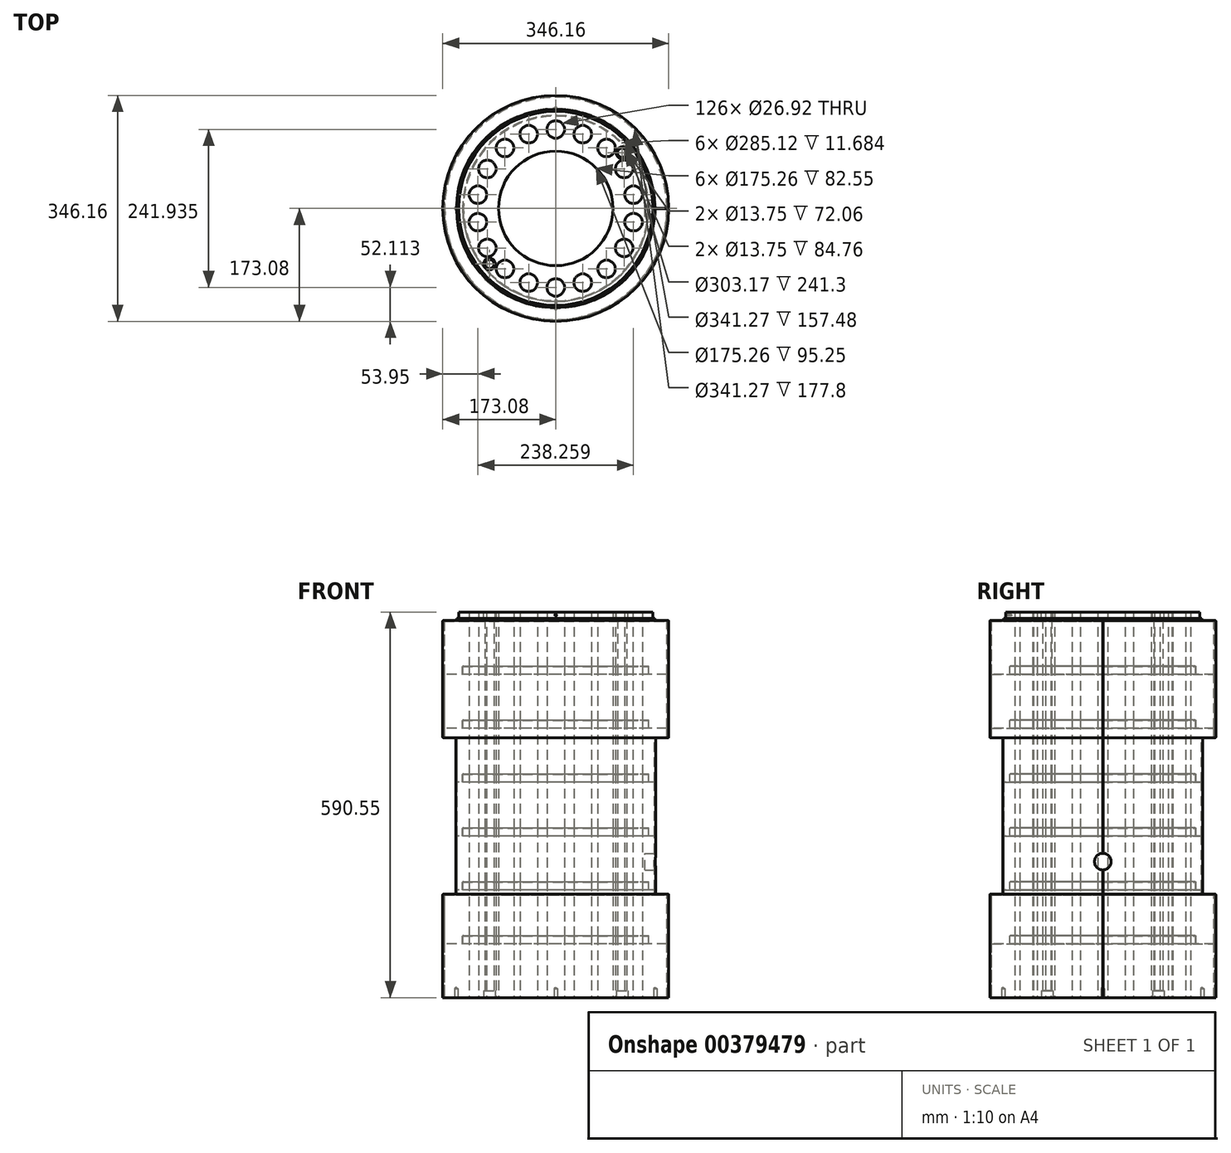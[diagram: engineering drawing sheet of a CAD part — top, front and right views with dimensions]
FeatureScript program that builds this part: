
annotation { "Feature Type Name" : "Feature", "Feature Type Description" : "" }
export const myFeature = defineFeature(function(context is Context, id is Id, definition is map)
    precondition{}
    {
        {
            var Q0;
            Q0=qCreatedBy(makeId("Right.planeOp"),FACE);
            var sketch = newSketch(context, id + "F0", { "sketchPlane" : qUnion([Q0])});
            skLineSegment(sketch, "E0", {"start": v(0, 0) * mm, "end": v(170.18, 0) * mm});
            skLineSegment(sketch, "E1", {"start": v(170.18, 157.48) * mm, "end": v(151.13, 157.48) * mm});
            skLineSegment(sketch, "E2", {"start": v(151.13, 157.48) * mm, "end": v(151.13, 398.78) * mm});
            skLineSegment(sketch, "E3", {"start": v(151.13, 398.78) * mm, "end": v(170.18, 398.78) * mm});
            skLineSegment(sketch, "E4", {"start": v(170.18, 398.78) * mm, "end": v(170.18, 576.58) * mm});
            skLineSegment(sketch, "E5", {"start": v(170.18, 576.58) * mm, "end": v(151.13, 576.58) * mm});
            skLineSegment(sketch, "E6", {"start": v(151.13, 576.58) * mm, "end": v(151.13, 581.03) * mm});
            skLineSegment(sketch, "E7", {"start": v(151.13, 581.03) * mm, "end": v(148.59, 581.03) * mm});
            skLineSegment(sketch, "E8", {"start": v(148.59, 581.03) * mm, "end": v(148.59, 590.55) * mm});
            skLineSegment(sketch, "E9", {"start": v(148.59, 590.55) * mm, "end": v(0, 590.55) * mm});
            skLineSegment(sketch, "E10", {"start": v(0, 590.55) * mm, "end": v(0, 0) * mm});
            skLineSegment(sketch, "E11", {"start": v(170.18, 82.55) * mm, "end": v(142.43, 82.55) * mm});
            skLineSegment(sketch, "E12", {"start": v(142.43, 82.55) * mm, "end": v(142.43, 95.25) * mm});
            skLineSegment(sketch, "E13", {"start": v(142.43, 95.25) * mm, "end": v(0, 95.25) * mm});
            skLineSegment(sketch, "E14", {"start": v(151.13, 165.1) * mm, "end": v(142.43, 165.1) * mm});
            skLineSegment(sketch, "E15", {"start": v(142.43, 165.1) * mm, "end": v(142.43, 177.8) * mm});
            skLineSegment(sketch, "E16", {"start": v(142.43, 177.8) * mm, "end": v(0, 177.8) * mm});
            skLineSegment(sketch, "E17", {"start": v(142.56, 82.55) * mm, "end": v(142.43, 82.55) * mm});
            skLineSegment(sketch, "E18", {"start": v(142.56, 82.55) * mm, "end": v(142.56, 95.25) * mm});
            skLineSegment(sketch, "E19", {"start": v(142.43, 165.1) * mm, "end": v(142.43, 165.1) * mm});
            skLineSegment(sketch, "E20", {"start": v(142.56, 95.25) * mm, "end": v(142.43, 95.25) * mm});
            skLineSegment(sketch, "E21", {"start": v(142.43, 177.8) * mm, "end": v(142.56, 177.8) * mm});
            skLineSegment(sketch, "E22", {"start": v(142.56, 177.8) * mm, "end": v(142.56, 165.1) * mm});
            skLineSegment(sketch, "E23", {"start": v(170.18, 412.75) * mm, "end": v(142.56, 412.75) * mm});
            skLineSegment(sketch, "E24", {"start": v(142.56, 412.75) * mm, "end": v(142.56, 425.45) * mm});
            skLineSegment(sketch, "E25", {"start": v(142.56, 425.45) * mm, "end": v(0, 425.45) * mm});
            skLineSegment(sketch, "E26", {"start": v(142.56, 412.75) * mm, "end": v(142.43, 412.75) * mm});
            skLineSegment(sketch, "E27", {"start": v(142.43, 412.75) * mm, "end": v(142.43, 425.45) * mm});
            skLineSegment(sketch, "E28", {"start": v(170.18, 495.3) * mm, "end": v(142.56, 495.3) * mm});
            skLineSegment(sketch, "E29", {"start": v(142.56, 495.3) * mm, "end": v(142.56, 508) * mm});
            skLineSegment(sketch, "E30", {"start": v(142.56, 508) * mm, "end": v(0, 508) * mm});
            skLineSegment(sketch, "E31", {"start": v(142.56, 495.3) * mm, "end": v(142.43, 495.3) * mm});
            skLineSegment(sketch, "E32", {"start": v(142.43, 495.3) * mm, "end": v(142.43, 508) * mm});
            skLineSegment(sketch, "E33", {"start": v(170.18, 0) * mm, "end": v(170.18, 82.55) * mm});
            skLineSegment(sketch, "E34", {"start": v(170.18, 82.55) * mm, "end": v(170.18, 157.48) * mm});
            skPoint(sketch, "E35.end.orphan", {"position": v(0, 177.8) * mm});
            skPoint(sketch, "E36.orphan", {"position": v(151.13, 165.1) * mm});
            skLineSegment(sketch, "E37", {"start": v(151.13, 247.65) * mm, "end": v(142.43, 247.65) * mm});
            skLineSegment(sketch, "E38", {"start": v(142.43, 247.65) * mm, "end": v(142.43, 260.35) * mm});
            skLineSegment(sketch, "E39", {"start": v(142.43, 260.35) * mm, "end": v(0, 260.35) * mm});
            skLineSegment(sketch, "E40", {"start": v(142.43, 260.35) * mm, "end": v(142.56, 260.35) * mm});
            skLineSegment(sketch, "E41", {"start": v(142.56, 260.35) * mm, "end": v(142.56, 247.65) * mm});
            skLineSegment(sketch, "E42", {"start": v(151.13, 330.2) * mm, "end": v(142.43, 330.2) * mm});
            skLineSegment(sketch, "E43", {"start": v(142.43, 330.2) * mm, "end": v(142.43, 342.9) * mm});
            skLineSegment(sketch, "E44", {"start": v(142.43, 342.9) * mm, "end": v(0, 342.9) * mm});
            skLineSegment(sketch, "E45", {"start": v(142.43, 342.9) * mm, "end": v(142.56, 342.9) * mm});
            skLineSegment(sketch, "E46", {"start": v(142.56, 342.9) * mm, "end": v(142.56, 330.2) * mm});
            skSolve(sketch);
        }
        {
            var Q0;
            {var subQ0=sQuery(id+"F0.wireOp",EDGE,"E0");Q0=makeQuery(id+"F0.imprint","IMPRINT",FACE,{"disambiguationData":[TD([[makeQuery(id+"F0.imprint","IMPRINT",EDGE,{"derivedFrom":subQ0}),1.0]])]});}
            var Q1;
            Q1=sQuery(id+"F0.wireOp",EDGE,"E10");
            revolve(context, id + "F1", {"entities" : qUnion([Q0]), "axis" : qUnion([Q1]), "revolveType" : RevolveType.FULL});
        }
        {
            var Q0;
            {var subQ6=sQuery(id+"F0.wireOp",EDGE,"E1");Q0=makeQuery(id+"F0.imprint","IMPRINT",FACE,{"disambiguationData":[TD([[makeQuery(id+"F0.imprint","IMPRINT",EDGE,{"derivedFrom":subQ6}),1.0]])]});}
            var Q1;
            Q1=sQuery(id+"F0.wireOp",EDGE,"E10");
            revolve(context, id + "F2", {"entities" : qUnion([Q0]), "axis" : qUnion([Q1]), "revolveType" : RevolveType.FULL});
        }
        {
            var Q0;
            {var subQ0=sQuery(id+"F0.wireOp",EDGE,"E16");Q0=makeQuery(id+"F0.imprint","IMPRINT",FACE,{"disambiguationData":[TD([[makeQuery(id+"F0.imprint","IMPRINT",EDGE,{"derivedFrom":subQ0}),-1.0]])]});}
            var Q1;
            Q1=sQuery(id+"F0.wireOp",EDGE,"E10");
            revolve(context, id + "F3", {"entities" : qUnion([Q0]), "axis" : qUnion([Q1]), "revolveType" : RevolveType.FULL});
        }
        {
            var Q0;
            {var subQ0=sQuery(id+"F0.wireOp",EDGE,"E39");Q0=makeQuery(id+"F0.imprint","IMPRINT",FACE,{"disambiguationData":[TD([[makeQuery(id+"F0.imprint","IMPRINT",EDGE,{"derivedFrom":subQ0}),-1.0]])]});}
            var Q1;
            Q1=sQuery(id+"F0.wireOp",EDGE,"E10");
            revolve(context, id + "F4", {"entities" : qUnion([Q0]), "axis" : qUnion([Q1]), "revolveType" : RevolveType.FULL});
        }
        {
            var Q0;
            {var subQ10=sQuery(id+"F0.wireOp",EDGE,"E3");Q0=makeQuery(id+"F0.imprint","IMPRINT",FACE,{"disambiguationData":[TD([[makeQuery(id+"F0.imprint","IMPRINT",EDGE,{"derivedFrom":subQ10}),1.0]])]});}
            var Q1;
            Q1=sQuery(id+"F0.wireOp",EDGE,"E10");
            revolve(context, id + "F5", {"entities" : qUnion([Q0]), "axis" : qUnion([Q1]), "revolveType" : RevolveType.FULL});
        }
        {
            var Q0;
            {var subQ1=sQuery(id+"F0.wireOp",EDGE,"E23");Q0=makeQuery(id+"F0.imprint","IMPRINT",FACE,{"disambiguationData":[TD([[makeQuery(id+"F0.imprint","IMPRINT",EDGE,{"derivedFrom":subQ1}),-1.0]])]});}
            var Q1;
            Q1=sQuery(id+"F0.wireOp",EDGE,"E10");
            revolve(context, id + "F6", {"entities" : qUnion([Q0]), "axis" : qUnion([Q1]), "revolveType" : RevolveType.FULL});
        }
        {
            var Q0;
            {var subQ7=sQuery(id+"F0.wireOp",EDGE,"E5");Q0=makeQuery(id+"F0.imprint","IMPRINT",FACE,{"disambiguationData":[TD([[makeQuery(id+"F0.imprint","IMPRINT",EDGE,{"derivedFrom":subQ7}),1.0]])]});}
            var Q1;
            Q1=sQuery(id+"F0.wireOp",EDGE,"E10");
            revolve(context, id + "F7", {"entities" : qUnion([Q0]), "axis" : qUnion([Q1]), "revolveType" : RevolveType.FULL});
        }
        {
            var Q0;
            Q0=makeQuery(id+"F1.opRevolve","SWEPT_FACE",FACE,{"disambiguationData":[OSD([sQuery(id+"F0.wireOp",EDGE,"E0")])]});
            var sketch = newSketch(context, id + "F8", { "sketchPlane" : qUnion([Q0])});
            skCircle(sketch, "E47", {"center": v(0, 0) * mm, "radius": 87.63 * mm});
            skCircle(sketch, "E48", {"center": v(0, -120.97) * mm, "radius": 13.46 * mm});
            skCircle(sketch, "E49", {"center": v(0, 0) * mm, "radius": 120.97 * mm, "construction": true});
            skCircle(sketch, "E50.1.0", {"center": v(41.37, -113.67) * mm, "radius": 13.46 * mm});
            skCircle(sketch, "E50.2.0", {"center": v(77.76, -92.67) * mm, "radius": 13.46 * mm});
            skCircle(sketch, "E50.3.0", {"center": v(104.76, -60.48) * mm, "radius": 13.46 * mm});
            skCircle(sketch, "E50.4.0", {"center": v(119.13, -21) * mm, "radius": 13.46 * mm});
            skCircle(sketch, "E50.5.0", {"center": v(119.13, 21) * mm, "radius": 13.46 * mm});
            skCircle(sketch, "E50.6.0", {"center": v(104.76, 60.48) * mm, "radius": 13.46 * mm});
            skCircle(sketch, "E50.7.0", {"center": v(77.76, 92.67) * mm, "radius": 13.46 * mm});
            skCircle(sketch, "E50.8.0", {"center": v(41.37, 113.67) * mm, "radius": 13.46 * mm});
            skCircle(sketch, "E50.9.0", {"center": v(0, 120.97) * mm, "radius": 13.46 * mm});
            skCircle(sketch, "E50.10.0", {"center": v(-41.37, 113.67) * mm, "radius": 13.46 * mm});
            skCircle(sketch, "E50.11.0", {"center": v(-77.76, 92.67) * mm, "radius": 13.46 * mm});
            skCircle(sketch, "E50.12.0", {"center": v(-104.76, 60.48) * mm, "radius": 13.46 * mm});
            skCircle(sketch, "E50.13.0", {"center": v(-119.13, 21) * mm, "radius": 13.46 * mm});
            skCircle(sketch, "E50.14.0", {"center": v(-119.13, -21) * mm, "radius": 13.46 * mm});
            skCircle(sketch, "E50.15.0", {"center": v(-104.76, -60.48) * mm, "radius": 13.46 * mm});
            skCircle(sketch, "E50.16.0", {"center": v(-77.76, -92.67) * mm, "radius": 13.46 * mm});
            skCircle(sketch, "E50.17.0", {"center": v(-41.37, -113.67) * mm, "radius": 13.46 * mm});
            skLineSegment(sketch, "E51", {"start": v(0, 0) * mm, "end": v(101.5, -85.17) * mm, "construction": true});
            skCircle(sketch, "E52", {"center": v(0, 0) * mm, "radius": 132.5 * mm, "construction": true});
            skCircle(sketch, "E53", {"center": v(101.5, -85.17) * mm, "radius": 6.87 * mm});
            skCircle(sketch, "E54.1.0", {"center": v(-101.5, 85.17) * mm, "radius": 6.87 * mm});
            skLineSegment(sketch, "E55", {"start": v(0, 0) * mm, "end": v(0, -120.97) * mm, "construction": true});
            skSolve(sketch);
        }
        {
            var Q0;
            Q0=makeQuery(id+"F8.imprint","IMPRINT",FACE,{"disambiguationData":[TD([[makeQuery(id+"F8.imprint","IMPRINT",EDGE,{"derivedFrom":sQuery(id+"F8.wireOp",EDGE,"E47")}),1.0]])]});
            var Q1;
            Q1=makeQuery(id+"F8.imprint","IMPRINT",FACE,{"disambiguationData":[TD([[makeQuery(id+"F8.imprint","IMPRINT",EDGE,{"derivedFrom":sQuery(id+"F8.wireOp",EDGE,"E48")}),1.0]])]});
            var Q2;
            Q2=makeQuery(id+"F8.imprint","IMPRINT",FACE,{"disambiguationData":[TD([[makeQuery(id+"F8.imprint","IMPRINT",EDGE,{"derivedFrom":sQuery(id+"F8.wireOp",EDGE,"E50.1.0")}),1.0]])]});
            var Q3;
            Q3=makeQuery(id+"F8.imprint","IMPRINT",FACE,{"disambiguationData":[TD([[makeQuery(id+"F8.imprint","IMPRINT",EDGE,{"derivedFrom":sQuery(id+"F8.wireOp",EDGE,"E50.17.0")}),1.0]])]});
            var Q4;
            Q4=makeQuery(id+"F8.imprint","IMPRINT",FACE,{"disambiguationData":[TD([[makeQuery(id+"F8.imprint","IMPRINT",EDGE,{"derivedFrom":sQuery(id+"F8.wireOp",EDGE,"E50.16.0")}),1.0]])]});
            var Q5;
            Q5=makeQuery(id+"F8.imprint","IMPRINT",FACE,{"disambiguationData":[TD([[makeQuery(id+"F8.imprint","IMPRINT",EDGE,{"derivedFrom":sQuery(id+"F8.wireOp",EDGE,"E53")}),1.0]])]});
            var Q6;
            Q6=makeQuery(id+"F8.imprint","IMPRINT",FACE,{"disambiguationData":[TD([[makeQuery(id+"F8.imprint","IMPRINT",EDGE,{"derivedFrom":sQuery(id+"F8.wireOp",EDGE,"E50.15.0")}),1.0]])]});
            var Q7;
            Q7=makeQuery(id+"F8.imprint","IMPRINT",FACE,{"disambiguationData":[TD([[makeQuery(id+"F8.imprint","IMPRINT",EDGE,{"derivedFrom":sQuery(id+"F8.wireOp",EDGE,"E50.14.0")}),1.0]])]});
            var Q8;
            Q8=makeQuery(id+"F8.imprint","IMPRINT",FACE,{"disambiguationData":[TD([[makeQuery(id+"F8.imprint","IMPRINT",EDGE,{"derivedFrom":sQuery(id+"F8.wireOp",EDGE,"E50.13.0")}),1.0]])]});
            var Q9;
            Q9=makeQuery(id+"F8.imprint","IMPRINT",FACE,{"disambiguationData":[TD([[makeQuery(id+"F8.imprint","IMPRINT",EDGE,{"derivedFrom":sQuery(id+"F8.wireOp",EDGE,"E50.12.0")}),1.0]])]});
            var Q10;
            Q10=makeQuery(id+"F8.imprint","IMPRINT",FACE,{"disambiguationData":[TD([[makeQuery(id+"F8.imprint","IMPRINT",EDGE,{"derivedFrom":sQuery(id+"F8.wireOp",EDGE,"E50.10.0")}),1.0]])]});
            var Q11;
            Q11=makeQuery(id+"F8.imprint","IMPRINT",FACE,{"disambiguationData":[TD([[makeQuery(id+"F8.imprint","IMPRINT",EDGE,{"derivedFrom":sQuery(id+"F8.wireOp",EDGE,"E50.9.0")}),1.0]])]});
            var Q12;
            Q12=makeQuery(id+"F8.imprint","IMPRINT",FACE,{"disambiguationData":[TD([[makeQuery(id+"F8.imprint","IMPRINT",EDGE,{"derivedFrom":sQuery(id+"F8.wireOp",EDGE,"E50.8.0")}),1.0]])]});
            var Q13;
            Q13=makeQuery(id+"F8.imprint","IMPRINT",FACE,{"disambiguationData":[TD([[makeQuery(id+"F8.imprint","IMPRINT",EDGE,{"derivedFrom":sQuery(id+"F8.wireOp",EDGE,"E50.6.0")}),1.0]])]});
            var Q14;
            Q14=makeQuery(id+"F8.imprint","IMPRINT",FACE,{"disambiguationData":[TD([[makeQuery(id+"F8.imprint","IMPRINT",EDGE,{"derivedFrom":sQuery(id+"F8.wireOp",EDGE,"E54.1.0")}),1.0]])]});
            var Q15;
            Q15=makeQuery(id+"F8.imprint","IMPRINT",FACE,{"disambiguationData":[TD([[makeQuery(id+"F8.imprint","IMPRINT",EDGE,{"derivedFrom":sQuery(id+"F8.wireOp",EDGE,"E50.5.0")}),1.0]])]});
            var Q16;
            Q16=makeQuery(id+"F8.imprint","IMPRINT",FACE,{"disambiguationData":[TD([[makeQuery(id+"F8.imprint","IMPRINT",EDGE,{"derivedFrom":sQuery(id+"F8.wireOp",EDGE,"E50.4.0")}),1.0]])]});
            var Q17;
            Q17=makeQuery(id+"F8.imprint","IMPRINT",FACE,{"disambiguationData":[TD([[makeQuery(id+"F8.imprint","IMPRINT",EDGE,{"derivedFrom":sQuery(id+"F8.wireOp",EDGE,"E50.2.0")}),1.0]])]});
            var Q18;
            Q18=makeQuery(id+"F8.imprint","IMPRINT",FACE,{"disambiguationData":[TD([[makeQuery(id+"F8.imprint","IMPRINT",EDGE,{"derivedFrom":sQuery(id+"F8.wireOp",EDGE,"E50.3.0")}),1.0]])]});
            var Q19;
            Q19=makeQuery(id+"F8.imprint","IMPRINT",FACE,{"disambiguationData":[TD([[makeQuery(id+"F8.imprint","IMPRINT",EDGE,{"derivedFrom":sQuery(id+"F8.wireOp",EDGE,"E50.11.0")}),1.0]])]});
            var Q20;
            Q20=makeQuery(id+"F8.imprint","IMPRINT",FACE,{"disambiguationData":[TD([[makeQuery(id+"F8.imprint","IMPRINT",EDGE,{"derivedFrom":sQuery(id+"F8.wireOp",EDGE,"E50.7.0")}),1.0]])]});
            var Q21;
            Q21=makeQuery(id+"F7.opRevolve","SWEPT_FACE",FACE,{"disambiguationData":[OSD([sQuery(id+"F0.wireOp",EDGE,"E9")])]});
            extrude(context, id + "F9", {"entities" : qUnion([Q0, Q1, Q2, Q3, Q4, Q5, Q6, Q7, Q8, Q9, Q10, Q11, Q12, Q13, Q14, Q15, Q16, Q17, Q18, Q19, Q20]), "operationType" : NewBodyOperationType.REMOVE, "endBound" : BoundingType.UP_TO_SURFACE, "oppositeDirection" : true, "endBoundEntityFace" : qUnion([Q21]), "depth" : 25.4 * mm});
        }
        {
            var Q0;
            Q0=makeQuery(id+"F1.opRevolve","SWEPT_EDGE",EDGE,{"disambiguationData":[OSD([sQuery(id+"F0.wireOp",EDGE,"E12"),sQuery(id+"F0.wireOp",EDGE,"E13"),sQuery(id+"F0.wireOp",EDGE,"E20")])]});
            chamfer(context, id + "F10", {"entities" : qUnion([Q0]), "chamferType" : ChamferType.OFFSET_ANGLE, "width" : 1.02 * mm, "oppositeDirection" : false, "angle" : 45 * degree, "tangentPropagation" : true});
        }
        {
            var Q0;
            Q0=makeQuery(id+"F2.opRevolve","SWEPT_EDGE",EDGE,{"disambiguationData":[OSD([sQuery(id+"F0.wireOp",EDGE,"E16"),sQuery(id+"F0.wireOp",EDGE,"E15"),sQuery(id+"F0.wireOp",EDGE,"E21")])]});
            var Q1;
            Q1=makeQuery(id+"F2.opRevolve","SWEPT_EDGE",EDGE,{"disambiguationData":[OSD([sQuery(id+"F0.wireOp",EDGE,"E18"),sQuery(id+"F0.wireOp",EDGE,"E20")])]});
            chamfer(context, id + "F11", {"entities" : qUnion([Q0, Q1]), "chamferType" : ChamferType.OFFSET_ANGLE, "width" : 1.02 * mm, "oppositeDirection" : false, "angle" : 45 * degree, "tangentPropagation" : true});
        }
        {
            var Q0;
            Q0=makeQuery(id+"F3.opRevolve","SWEPT_EDGE",EDGE,{"disambiguationData":[OSD([sQuery(id+"F0.wireOp",EDGE,"E38"),sQuery(id+"F0.wireOp",EDGE,"E39"),sQuery(id+"F0.wireOp",EDGE,"E40")])]});
            var Q1;
            Q1=makeQuery(id+"F3.opRevolve","SWEPT_EDGE",EDGE,{"disambiguationData":[OSD([sQuery(id+"F0.wireOp",EDGE,"E21"),sQuery(id+"F0.wireOp",EDGE,"E22")])]});
            chamfer(context, id + "F12", {"entities" : qUnion([Q0, Q1]), "chamferType" : ChamferType.OFFSET_ANGLE, "width" : 1.02 * mm, "oppositeDirection" : false, "angle" : 45 * degree, "tangentPropagation" : true});
        }
        {
            var Q0;
            Q0=makeQuery(id+"F4.opRevolve","SWEPT_EDGE",EDGE,{"disambiguationData":[OSD([sQuery(id+"F0.wireOp",EDGE,"E40"),sQuery(id+"F0.wireOp",EDGE,"E41")])]});
            var Q1;
            Q1=makeQuery(id+"F4.opRevolve","SWEPT_EDGE",EDGE,{"disambiguationData":[OSD([sQuery(id+"F0.wireOp",EDGE,"E43"),sQuery(id+"F0.wireOp",EDGE,"E44"),sQuery(id+"F0.wireOp",EDGE,"E45")])]});
            chamfer(context, id + "F13", {"entities" : qUnion([Q0, Q1]), "chamferType" : ChamferType.OFFSET_ANGLE, "width" : 1.02 * mm, "oppositeDirection" : false, "angle" : 45 * degree, "tangentPropagation" : true});
        }
        {
            var Q0;
            Q0=makeQuery(id+"F5.opRevolve","SWEPT_EDGE",EDGE,{"disambiguationData":[OSD([sQuery(id+"F0.wireOp",EDGE,"E25"),sQuery(id+"F0.wireOp",EDGE,"E27")])]});
            var Q1;
            Q1=makeQuery(id+"F5.opRevolve","SWEPT_EDGE",EDGE,{"disambiguationData":[OSD([sQuery(id+"F0.wireOp",EDGE,"E45"),sQuery(id+"F0.wireOp",EDGE,"E46")])]});
            chamfer(context, id + "F14", {"entities" : qUnion([Q0, Q1]), "chamferType" : ChamferType.OFFSET_ANGLE, "width" : 1.02 * mm, "oppositeDirection" : false, "angle" : 45 * degree, "tangentPropagation" : true});
        }
        {
            var Q0;
            Q0=makeQuery(id+"F6.opRevolve","SWEPT_EDGE",EDGE,{"disambiguationData":[OSD([sQuery(id+"F0.wireOp",EDGE,"E24"),sQuery(id+"F0.wireOp",EDGE,"E25")])]});
            var Q1;
            Q1=makeQuery(id+"F6.opRevolve","SWEPT_EDGE",EDGE,{"disambiguationData":[OSD([sQuery(id+"F0.wireOp",EDGE,"E30"),sQuery(id+"F0.wireOp",EDGE,"E32")])]});
            chamfer(context, id + "F15", {"entities" : qUnion([Q0, Q1]), "chamferType" : ChamferType.OFFSET_ANGLE, "width" : 1.02 * mm, "oppositeDirection" : false, "angle" : 45 * degree, "tangentPropagation" : true});
        }
        {
            var Q0;
            Q0=makeQuery(id+"F7.opRevolve","SWEPT_EDGE",EDGE,{"disambiguationData":[OSD([sQuery(id+"F0.wireOp",EDGE,"E29"),sQuery(id+"F0.wireOp",EDGE,"E30")])]});
            chamfer(context, id + "F16", {"entities" : qUnion([Q0]), "chamferType" : ChamferType.OFFSET_ANGLE, "width" : 1.02 * mm, "oppositeDirection" : false, "angle" : 45 * degree, "tangentPropagation" : true});
        }
        {
            var Q0;
            Q0=makeQuery(id+"F1.opRevolve","SWEPT_FACE",FACE,{"disambiguationData":[OSD([sQuery(id+"F0.wireOp",EDGE,"E0")])]});
            var sketch = newSketch(context, id + "F17", { "sketchPlane" : qUnion([Q0])});
            skPoint(sketch, "E56", {"position": v(0, 152.4) * mm});
            skPoint(sketch, "E57.1.0", {"position": v(-152.4, 0) * mm});
            skPoint(sketch, "E57.2.0", {"position": v(0, -152.4) * mm});
            skPoint(sketch, "E57.3.0", {"position": v(152.4, 0) * mm});
            skPoint(sketch, "E57.center", {"position": v(0, 0) * mm});
            skSolve(sketch);
        }
        {
            var Q0;
            Q0=sQuery(id+"F17.wireOp",VERTEX,"E56");
            var Q1;
            Q1=sQuery(id+"F17.wireOp",VERTEX,"E57.3.0");
            var Q2;
            Q2=sQuery(id+"F17.wireOp",VERTEX,"E57.2.0");
            var Q3;
            Q3=sQuery(id+"F17.wireOp",VERTEX,"E57.1.0");
            var Q4;
            Q4=makeQuery(id+"F1.opRevolve","SWEPT_BODY",BODY,{"disambiguationData":[OSD([sQuery(id+"F0.wireOp",EDGE,"E0"),sQuery(id+"F0.wireOp",EDGE,"E10"),sQuery(id+"F0.wireOp",EDGE,"E11"),sQuery(id+"F0.wireOp",EDGE,"E12"),sQuery(id+"F0.wireOp",EDGE,"E13"),sQuery(id+"F0.wireOp",EDGE,"E17"),sQuery(id+"F0.wireOp",EDGE,"E33")])]});
            hole(context, id + "F18", {"style" : HoleStyle.SIMPLE, "endStyle" : HoleEndStyle.BLIND, "standardTappedOrClearance" : lookupTablePath({ "standard" : "ANSI", "engagement" : "75%", "pitch" : "20 tpi", "size" : "1/4", "type" : "Tapped" }), "standardBlindInLast" : lookupTablePath({ "standard" : "ANSI", "engagement" : "75%", "pitch" : "20 tpi", "size" : "1/4", "type" : "Tapped" }), "holeDiameter" : 5.1 * mm, "showTappedDepth" : true, "holeDepth" : 13.97 * mm, "tappedDepth" : 12.7 * mm, "tapClearance" : 1, "locations" : qUnion([Q0, Q1, Q2, Q3]), "scope" : qUnion([Q4]), "majorDiameter" : 6.35 * mm});
        }
        {
            var Q0;
            Q0=makeQuery(id+"F1.opRevolve","SWEPT_FACE",FACE,{"disambiguationData":[OSD([sQuery(id+"F0.wireOp",EDGE,"E0")])]});
            var sketch = newSketch(context, id + "F19", { "sketchPlane" : qUnion([Q0])});
            skCircle(sketch, "E58", {"center": v(-101.5, 85.17) * mm, "radius": 9 * mm});
            skCircle(sketch, "E59", {"center": v(101.5, -85.17) * mm, "radius": 9 * mm});
            skSolve(sketch);
        }
        {
            var Q0;
            Q0=makeQuery(id+"F19.imprint","IMPRINT",FACE,{"disambiguationData":[TD([[makeQuery(id+"F19.imprint","IMPRINT",EDGE,{"derivedFrom":sQuery(id+"F19.wireOp",EDGE,"E58")}),1.0]])]});
            var Q1;
            Q1=makeQuery(id+"F19.imprint","IMPRINT",FACE,{"disambiguationData":[TD([[makeQuery(id+"F19.imprint","IMPRINT",EDGE,{"derivedFrom":sQuery(id+"F19.wireOp",EDGE,"E59")}),1.0]])]});
            extrude(context, id + "F20", {"entities" : qUnion([Q0, Q1]), "operationType" : NewBodyOperationType.REMOVE, "oppositeDirection" : true, "depth" : 10.5 * mm});
        }
        {
            var Q0;
            Q0=makeQuery(id+"F7.opRevolve","SWEPT_FACE",FACE,{"disambiguationData":[OSD([sQuery(id+"F0.wireOp",EDGE,"E9")])]});
            var sketch = newSketch(context, id + "F21", { "sketchPlane" : qUnion([Q0])});
            skCircle(sketch, "E60", {"center": v(-101.5, -85.17) * mm, "radius": 9 * mm});
            skCircle(sketch, "E61", {"center": v(101.5, 85.17) * mm, "radius": 9 * mm});
            skSolve(sketch);
        }
        {
            var Q0;
            Q0=makeQuery(id+"F21.imprint","IMPRINT",FACE,{"disambiguationData":[TD([[makeQuery(id+"F21.imprint","IMPRINT",EDGE,{"derivedFrom":sQuery(id+"F21.wireOp",EDGE,"E61")}),1.0]])]});
            var Q1;
            Q1=makeQuery(id+"F21.imprint","IMPRINT",FACE,{"disambiguationData":[TD([[makeQuery(id+"F21.imprint","IMPRINT",EDGE,{"derivedFrom":sQuery(id+"F21.wireOp",EDGE,"E60")}),1.0]])]});
            extrude(context, id + "F22", {"entities" : qUnion([Q0, Q1]), "operationType" : NewBodyOperationType.REMOVE, "oppositeDirection" : true, "depth" : 10.5 * mm});
        }
        {
            var Q0;
            Q0=qCreatedBy(makeId("Front.planeOp"),FACE);
            cPlane(context, id + "F23", {"entities" : qUnion([Q0]), "cplaneType" : CPlaneType.OFFSET, "offset" : 148.6 * mm, "width" : 152.4 * mm, "height" : 152.4 * mm});
        }
        {
            var Q0;
            Q0=qCreatedBy(id+"F23.planeOp",FACE);
            var sketch = newSketch(context, id + "F24", { "sketchPlane" : qUnion([Q0])});
            skLineSegment(sketch, "E62", {"start": v(170.18, 576.58) * mm, "end": v(170.18, 495.3) * mm});
            skLineSegment(sketch, "E63", {"start": v(-170.18, 495.3) * mm, "end": v(-170.18, 576.58) * mm});
            skLineSegment(sketch, "E64", {"start": v(148.59, 590.55) * mm, "end": v(148.59, 581.03) * mm});
            skLineSegment(sketch, "E65", {"start": v(-148.59, 581.03) * mm, "end": v(-148.59, 590.55) * mm});
            skLineSegment(sketch, "E66.0", {"start": v(-151.13, 581.03) * mm, "end": v(151.13, 581.03) * mm});
            skLineSegment(sketch, "E67", {"start": v(151.13, 581.03) * mm, "end": v(151.13, 576.58) * mm});
            skLineSegment(sketch, "E68", {"start": v(-151.13, 576.58) * mm, "end": v(-151.13, 581.03) * mm});
            skPoint(sketch, "E69", {"position": v(0, 585.8) * mm});
            skPoint(sketch, "E69.positionSnap0", {"position": v(0, 581.03) * mm});
            skSolve(sketch);
        }
        {
            var Q0;
            Q0=sQuery(id+"F24.wireOp",VERTEX,"E69");
            var Q1;
            Q1=makeQuery(id+"F7.opRevolve","SWEPT_BODY",BODY,{"disambiguationData":[OSD([sQuery(id+"F0.wireOp",EDGE,"E4"),sQuery(id+"F0.wireOp",EDGE,"E5"),sQuery(id+"F0.wireOp",EDGE,"E6"),sQuery(id+"F0.wireOp",EDGE,"E7"),sQuery(id+"F0.wireOp",EDGE,"E8"),sQuery(id+"F0.wireOp",EDGE,"E9"),sQuery(id+"F0.wireOp",EDGE,"E10"),sQuery(id+"F0.wireOp",EDGE,"E28"),sQuery(id+"F0.wireOp",EDGE,"E29"),sQuery(id+"F0.wireOp",EDGE,"E30")])]});
            hole(context, id + "F25", {"style" : HoleStyle.SIMPLE, "endStyle" : HoleEndStyle.BLIND, "standardTappedOrClearance" : lookupTablePath({ "standard" : "ANSI", "engagement" : "75%", "pitch" : "32 tpi", "size" : "#6", "type" : "Tapped" }), "standardBlindInLast" : lookupTablePath({ "standard" : "ANSI", "engagement" : "75%", "pitch" : "32 tpi", "size" : "#6", "type" : "Tapped" }), "holeDiameter" : 2.7 * mm, "showTappedDepth" : true, "holeDepth" : 8.4 * mm, "tappedDepth" : 7.62 * mm, "tapClearance" : 1, "locations" : qUnion([Q0]), "scope" : qUnion([Q1]), "majorDiameter" : 3.5 * mm});
        }
        {
            var Q0;
            Q0=qCreatedBy(makeId("Front.planeOp"),FACE);
            var sketch = newSketch(context, id + "F26", { "sketchPlane" : qUnion([Q0])});
            skLineSegment(sketch, "E70.bottom", {"start": v(-171.45, 0) * mm, "end": v(-170.64, 0) * mm});
            skLineSegment(sketch, "E70.top", {"start": v(-171.45, 157.48) * mm, "end": v(-170.64, 157.48) * mm});
            skLineSegment(sketch, "E70.left", {"start": v(-171.45, 0) * mm, "end": v(-171.45, 157.48) * mm});
            skLineSegment(sketch, "E70.right", {"start": v(-170.64, 0) * mm, "end": v(-170.64, 157.48) * mm});
            skLineSegment(sketch, "E71.bottom", {"start": v(-152.4, 157.48) * mm, "end": v(-151.59, 157.48) * mm});
            skLineSegment(sketch, "E71.top", {"start": v(-152.4, 398.78) * mm, "end": v(-151.59, 398.78) * mm});
            skLineSegment(sketch, "E71.left", {"start": v(-152.4, 157.48) * mm, "end": v(-152.4, 398.78) * mm});
            skLineSegment(sketch, "E71.right", {"start": v(-151.59, 157.48) * mm, "end": v(-151.59, 398.78) * mm});
            skLineSegment(sketch, "E72.bottom", {"start": v(-171.45, 398.78) * mm, "end": v(-170.64, 398.78) * mm});
            skLineSegment(sketch, "E72.top", {"start": v(-171.45, 576.58) * mm, "end": v(-170.64, 576.58) * mm});
            skLineSegment(sketch, "E72.left", {"start": v(-171.45, 398.78) * mm, "end": v(-171.45, 576.58) * mm});
            skLineSegment(sketch, "E72.right", {"start": v(-170.64, 398.78) * mm, "end": v(-170.64, 576.58) * mm});
            skSolve(sketch);
        }
        {
            var Q0;
            Q0=makeQuery(id+"F26.imprint","IMPRINT",FACE,{"disambiguationData":[TD([[makeQuery(id+"F26.imprint","IMPRINT",EDGE,{"derivedFrom":sQuery(id+"F26.wireOp",EDGE,"E70.bottom")}),1.0]])]});
            var Q1;
            Q1=makeQuery(id+"F9.boolean.opBoolean","COPY",FACE,{"disambiguationData":[TD([makeQuery(id+"F1.opRevolve","SWEPT_FACE",FACE,{"disambiguationData":[OSD([sQuery(id+"F0.wireOp",EDGE,"E0")])]})])],"derivedFrom":makeQuery(id+"F9.opExtrude","SWEPT_FACE",FACE,{"disambiguationData":[OSD([sQuery(id+"F8.wireOp",EDGE,"E47")])]})});
            revolve(context, id + "F27", {"entities" : qUnion([Q0]), "axis" : qUnion([Q1]), "revolveType" : RevolveType.FULL});
        }
        {
            var Q0;
            Q0=makeQuery(id+"F26.imprint","IMPRINT",FACE,{"disambiguationData":[TD([[makeQuery(id+"F26.imprint","IMPRINT",EDGE,{"derivedFrom":sQuery(id+"F26.wireOp",EDGE,"E71.bottom")}),1.0]])]});
            var Q1;
            Q1=makeQuery(id+"F9.boolean.opBoolean","COPY",FACE,{"disambiguationData":[TD([makeQuery(id+"F1.opRevolve","SWEPT_FACE",FACE,{"disambiguationData":[OSD([sQuery(id+"F0.wireOp",EDGE,"E0")])]})])],"derivedFrom":makeQuery(id+"F9.opExtrude","SWEPT_FACE",FACE,{"disambiguationData":[OSD([sQuery(id+"F8.wireOp",EDGE,"E47")])]})});
            revolve(context, id + "F28", {"entities" : qUnion([Q0]), "axis" : qUnion([Q1]), "revolveType" : RevolveType.FULL});
        }
        {
            var Q0;
            Q0=makeQuery(id+"F26.imprint","IMPRINT",FACE,{"disambiguationData":[TD([[makeQuery(id+"F26.imprint","IMPRINT",EDGE,{"derivedFrom":sQuery(id+"F26.wireOp",EDGE,"E72.bottom")}),1.0]])]});
            var Q1;
            Q1=makeQuery(id+"F9.boolean.opBoolean","COPY",FACE,{"disambiguationData":[TD([makeQuery(id+"F1.opRevolve","SWEPT_FACE",FACE,{"disambiguationData":[OSD([sQuery(id+"F0.wireOp",EDGE,"E0")])]})])],"derivedFrom":makeQuery(id+"F9.opExtrude","SWEPT_FACE",FACE,{"disambiguationData":[OSD([sQuery(id+"F8.wireOp",EDGE,"E47")])]})});
            revolve(context, id + "F29", {"entities" : qUnion([Q0]), "axis" : qUnion([Q1]), "revolveType" : RevolveType.FULL});
        }
        {
            var Q0;
            Q0=qCreatedBy(makeId("Front.planeOp"),FACE);
            var sketch = newSketch(context, id + "F30", { "sketchPlane" : qUnion([Q0])});
            skLineSegment(sketch, "E73", {"start": v(-172.26, 0) * mm, "end": v(-172.26, 156.72) * mm});
            skLineSegment(sketch, "E74", {"start": v(-171.5, 157.48) * mm, "end": v(-153.16, 157.48) * mm});
            skLineSegment(sketch, "E75", {"start": v(-152.4, 158.24) * mm, "end": v(-152.4, 398.02) * mm});
            skLineSegment(sketch, "E76", {"start": v(-153.16, 398.78) * mm, "end": v(-171.5, 398.78) * mm});
            skLineSegment(sketch, "E77", {"start": v(-172.26, 399.54) * mm, "end": v(-172.26, 575.82) * mm});
            skLineSegment(sketch, "E78", {"start": v(-171.5, 576.58) * mm, "end": v(-151.9, 576.58) * mm});
            skLineSegment(sketch, "E79", {"start": v(-151.13, 577.34) * mm, "end": v(-151.13, 581.02) * mm});
            skLineSegment(sketch, "E80", {"start": v(-171.45, 398.78) * mm, "end": v(-171.45, 576.58) * mm});
            skLineSegment(sketch, "E81", {"start": v(171.45, 576.58) * mm, "end": v(171.45, 398.78) * mm});
            skLineSegment(sketch, "E82", {"start": v(-152.4, 157.48) * mm, "end": v(-152.4, 398.78) * mm});
            skLineSegment(sketch, "E83", {"start": v(152.4, 398.78) * mm, "end": v(152.4, 157.48) * mm});
            skLineSegment(sketch, "E84.0", {"start": v(-151.94, 578.15) * mm, "end": v(-151.94, 581.02) * mm});
            skLineSegment(sketch, "E84.1", {"start": v(-172.31, 577.4) * mm, "end": v(-152.7, 577.4) * mm});
            skLineSegment(sketch, "E84.2", {"start": v(-173.08, 398.73) * mm, "end": v(-173.08, 576.63) * mm});
            skLineSegment(sketch, "E84.3", {"start": v(-173.08, 0) * mm, "end": v(-173.08, 157.53) * mm});
            skLineSegment(sketch, "E84.4", {"start": v(-172.31, 158.3) * mm, "end": v(-153.97, 158.3) * mm});
            skLineSegment(sketch, "E84.5", {"start": v(-153.21, 159.05) * mm, "end": v(-153.21, 397.2) * mm});
            skLineSegment(sketch, "E84.6", {"start": v(-153.97, 397.97) * mm, "end": v(-172.31, 397.97) * mm});
            skLineSegment(sketch, "E85", {"start": v(-151.94, 581.02) * mm, "end": v(-151.13, 581.02) * mm});
            skLineSegment(sketch, "E86", {"start": v(-172.26, 0) * mm, "end": v(-173.08, 0) * mm});
            skPoint(sketch, "E87.visualSharp", {"position": v(-172.26, 157.48) * mm});
            skArc(sketch, "E87.filletArc", {"start": v(-171.5, 157.48) * mm, "mid": v(-172.04, 157.26) * mm, "end": v(-172.26, 156.72) * mm});
            skPoint(sketch, "E88.visualSharp", {"position": v(-173.08, 158.3) * mm});
            skArc(sketch, "E88.filletArc", {"start": v(-172.31, 158.3) * mm, "mid": v(-172.85, 158.07) * mm, "end": v(-173.08, 157.53) * mm});
            skPoint(sketch, "E89.visualSharp", {"position": v(-153.21, 158.3) * mm});
            skArc(sketch, "E89.filletArc", {"start": v(-153.97, 158.3) * mm, "mid": v(-153.44, 158.52) * mm, "end": v(-153.21, 159.05) * mm});
            skPoint(sketch, "E90.visualSharp", {"position": v(-152.4, 157.48) * mm});
            skArc(sketch, "E90.filletArc", {"start": v(-153.16, 157.48) * mm, "mid": v(-152.62, 157.7) * mm, "end": v(-152.4, 158.24) * mm});
            skPoint(sketch, "E91.visualSharp", {"position": v(-153.21, 397.97) * mm});
            skArc(sketch, "E91.filletArc", {"start": v(-153.21, 397.2) * mm, "mid": v(-153.44, 397.74) * mm, "end": v(-153.97, 397.97) * mm});
            skPoint(sketch, "E92.visualSharp", {"position": v(-152.4, 398.78) * mm});
            skArc(sketch, "E92.filletArc", {"start": v(-152.4, 398.02) * mm, "mid": v(-152.62, 398.56) * mm, "end": v(-153.16, 398.78) * mm});
            skPoint(sketch, "E93.visualSharp", {"position": v(-173.08, 397.97) * mm});
            skArc(sketch, "E93.filletArc", {"start": v(-173.08, 398.73) * mm, "mid": v(-172.85, 398.2) * mm, "end": v(-172.31, 397.97) * mm});
            skPoint(sketch, "E94.visualSharp", {"position": v(-172.26, 398.78) * mm});
            skArc(sketch, "E94.filletArc", {"start": v(-172.26, 399.54) * mm, "mid": v(-172.04, 399) * mm, "end": v(-171.5, 398.78) * mm});
            skPoint(sketch, "E95.visualSharp", {"position": v(-172.26, 576.58) * mm});
            skArc(sketch, "E95.filletArc", {"start": v(-171.5, 576.58) * mm, "mid": v(-172.04, 576.36) * mm, "end": v(-172.26, 575.82) * mm});
            skPoint(sketch, "E96.visualSharp", {"position": v(-173.08, 577.4) * mm});
            skArc(sketch, "E96.filletArc", {"start": v(-172.31, 577.4) * mm, "mid": v(-172.85, 577.17) * mm, "end": v(-173.08, 576.63) * mm});
            skPoint(sketch, "E97.visualSharp", {"position": v(-151.94, 577.4) * mm});
            skArc(sketch, "E97.filletArc", {"start": v(-152.7, 577.4) * mm, "mid": v(-152.17, 577.62) * mm, "end": v(-151.94, 578.15) * mm});
            skPoint(sketch, "E98.visualSharp", {"position": v(-151.13, 576.58) * mm});
            skArc(sketch, "E98.filletArc", {"start": v(-151.9, 576.58) * mm, "mid": v(-151.35, 576.8) * mm, "end": v(-151.13, 577.34) * mm});
            skSolve(sketch);
        }
        {
            var Q0;
            Q0=makeQuery(id+"F30.imprint","IMPRINT",FACE,{"disambiguationData":[TD([[makeQuery(id+"F30.imprint","IMPRINT",EDGE,{"derivedFrom":sQuery(id+"F30.wireOp",EDGE,"E73")}),1.0]])]});
            var Q1;
            Q1=makeQuery(id+"F9.boolean.opBoolean","COPY",FACE,{"disambiguationData":[TD([makeQuery(id+"F1.opRevolve","SWEPT_FACE",FACE,{"disambiguationData":[OSD([sQuery(id+"F0.wireOp",EDGE,"E0")])]})])],"derivedFrom":makeQuery(id+"F9.opExtrude","SWEPT_FACE",FACE,{"disambiguationData":[OSD([sQuery(id+"F8.wireOp",EDGE,"E47")])]})});
            revolve(context, id + "F31", {"entities" : qUnion([Q0]), "axis" : qUnion([Q1]), "revolveType" : RevolveType.TWO_DIRECTIONS, "angle" : 179.9 * degree, "angleBack" : 180.1 * degree});
        }
        {
            var Q0;
            Q0=qCreatedBy(makeId("Right.planeOp"),FACE);
            cPlane(context, id + "F32", {"entities" : qUnion([Q0]), "cplaneType" : CPlaneType.OFFSET, "offset" : 151.13 * mm, "width" : 152.4 * mm, "height" : 152.4 * mm});
        }
        {
            var Q0;
            Q0=qCreatedBy(id+"F32.planeOp",FACE);
            var sketch = newSketch(context, id + "F33", { "sketchPlane" : qUnion([Q0])});
            skLineSegment(sketch, "E99", {"start": v(151.13, 247.65) * mm, "end": v(151.13, 165.1) * mm, "construction": true});
            skLineSegment(sketch, "E100", {"start": v(-151.13, 165.1) * mm, "end": v(-151.13, 247.65) * mm, "construction": true});
            skCircle(sketch, "E101", {"center": v(0, 208.28) * mm, "radius": 12.7 * mm});
            skLineSegment(sketch, "E102.0", {"start": v(-151.13, 247.65) * mm, "end": v(151.13, 247.65) * mm, "construction": true});
            skLineSegment(sketch, "E103", {"start": v(-151.13, 165.1) * mm, "end": v(151.13, 165.1) * mm, "construction": true});
            skLineSegment(sketch, "E104", {"start": v(0, 165.1) * mm, "end": v(0, 247.65) * mm, "construction": true});
            skSolve(sketch);
        }
        {
            var Q0;
            Q0=makeQuery(id+"F33.imprint","IMPRINT",FACE,{"disambiguationData":[TD([[makeQuery(id+"F33.imprint","IMPRINT",EDGE,{"derivedFrom":sQuery(id+"F33.wireOp",EDGE,"E101")}),1.0]])]});
            extrude(context, id + "F34", {"entities" : qUnion([Q0]), "operationType" : NewBodyOperationType.REMOVE, "endBound" : BoundingType.SYMMETRIC, "oppositeDirection" : true, "depth" : 28.45 * mm});
        }
    });
